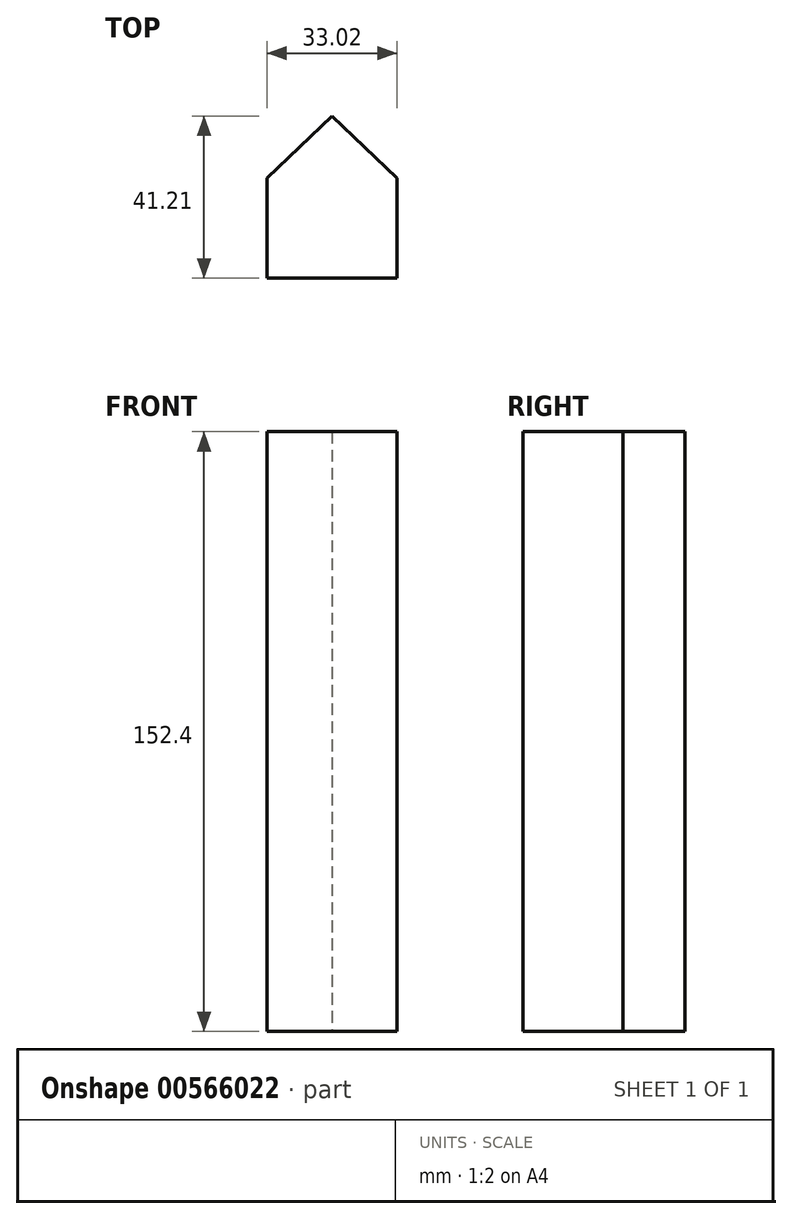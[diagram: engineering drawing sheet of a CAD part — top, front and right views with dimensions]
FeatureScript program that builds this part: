
annotation { "Feature Type Name" : "Feature", "Feature Type Description" : "" }
export const myFeature = defineFeature(function(context is Context, id is Id, definition is map)
    precondition{}
    {
        {
            var Q0;
            Q0=qCreatedBy(makeId("Top.planeOp"),FACE);
            var sketch = newSketch(context, id + "F0", { "sketchPlane" : qUnion([Q0])});
            skLineSegment(sketch, "E0.bottom", {"start": v(-18.3, 26.74) * mm, "end": v(-51.33, 26.74) * mm});
            skLineSegment(sketch, "E0.top", {"start": v(-18.3, 52.14) * mm, "end": v(-51.33, 52.14) * mm});
            skLineSegment(sketch, "E0.left", {"start": v(-18.3, 26.74) * mm, "end": v(-18.3, 52.14) * mm});
            skLineSegment(sketch, "E0.right", {"start": v(-51.33, 26.74) * mm, "end": v(-51.33, 52.14) * mm});
            skLineSegment(sketch, "E1", {"start": v(-51.33, 52.14) * mm, "end": v(-34.82, 67.95) * mm});
            skLineSegment(sketch, "E2", {"start": v(-34.82, 67.95) * mm, "end": v(-18.3, 52.14) * mm});
            skSolve(sketch);
        }
        {
            var Q0;
            Q0=makeQuery(id+"F0.imprint","IMPRINT",FACE,{"disambiguationData":[TD([[makeQuery(id+"F0.imprint","IMPRINT",EDGE,{"derivedFrom":sQuery(id+"F0.wireOp",EDGE,"E0.top")}),-1.0]])]});
            var Q1;
            Q1=makeQuery(id+"F0.imprint","IMPRINT",FACE,{"disambiguationData":[TD([[makeQuery(id+"F0.imprint","IMPRINT",EDGE,{"derivedFrom":sQuery(id+"F0.wireOp",EDGE,"E0.bottom")}),-1.0]])]});
            extrude(context, id + "F1", {"entities" : qUnion([Q0, Q1]), "depth" : 152.4 * mm, "offsetDistance" : 25.4 * mm});
        }
    });
